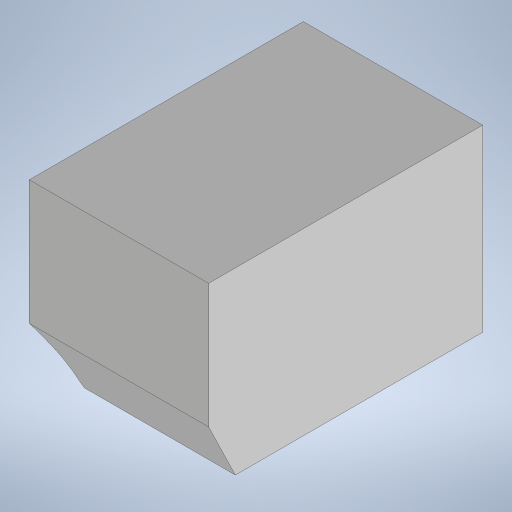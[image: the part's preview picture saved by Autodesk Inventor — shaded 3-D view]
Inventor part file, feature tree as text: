
AUTODESK INVENTOR PART (.ipt)
format: ipt  version: 2024 (Build 280153000, 153)  size: 10,664,960 bytes
history: native  units: mm
features: other x6, sketch x6, extrude x5, plane x2
ambient origin geometry x8: Origin, YZ Plane, XZ Plane, XY Plane, X Axis, Y Axis, Z Axis, Center Point
bodies: Body1 (feature_tree)
feature tree (19):
  other  "M.ipt"
  plane  "Plano de trabajo1"
  extrude  "Extrusión1"  [1 undecoded]
  other  "Combinar1"
  sketch  "Boceto3"  dims[d2=550.0mm d3=520.0mm]
  sketch  "Boceto4"  dims[d4=550.0mm d5=0.0mm d6=129.8482mm]
  plane  "Plano de trabajo2"
  sketch  "Boceto5"  dims[d17=180.0mm d18=180.0mm]
  extrude  "Extrusión2"  Depth=520.0mm
  extrude  "Extrusión3"  Depth=129.8482mm
  extrude  "Extrusión4"  Depth=180.0mm
  extrude  "Extrusión5"  Depth=180.0mm
  other  "Sólido1::M.ipt"
  other  "OperaciónIdentificador1"
  sketch  "Boceto1"  dims[d0=25.0mm d1=-365.0mm]
  other  "Sólido2"
  sketch  "Boceto6"  dims[d22=326.0mm d23=180.0mm]
  sketch  "Boceto7"  dims[d24=180.0mm d25=180.0mm d26=10.0mm d27=0.0mm d28=1000.0mm d29=0.0mm d30=30.0mm d31=30.0mm d32=16.0mm d33=16.0mm d34=0.0mm d35=30.0mm d36=30.0mm d37=16.0mm d38=16.0mm d39=0.0mm d14=0.5mm d15=0.872665mm d16=0.5mm d19=0.5mm d20=0.872665mm d21=0.5mm]
  other  "Sólido1"
note: 1 required parameter value undecoded (feature->parameter linkage not recoverable at this tier; creation-order binding heuristic only, values carry confidence <= 0.55)
